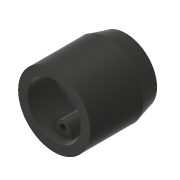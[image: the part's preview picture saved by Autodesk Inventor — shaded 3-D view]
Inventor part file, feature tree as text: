
AUTODESK INVENTOR PART (.ipt)
format: ipt  version: 2017 (Build 210142000, 142)  size: 183,296 bytes
history: native  units: in
note: dims shown in document units (in); Inventor stores cm internally (conversion verified against a paired STEP export)
features: extrude x9, sketch x9, reference x5, other x4, chamfer x1
ambient origin geometry x8: Origin, YZ Plane, XZ Plane, XY Plane, X Axis, Y Axis, Z Axis, Center Point
bodies: Solid1 (feature_tree)
feature tree (28):
  extrude  "Extrusion1"  Depth=1.0in TaperAngle=0.0deg
  extrude  "Extrusion3"  Depth=0.125in TaperAngle=0.0deg
  extrude  "Extrusion4"  Depth=0.75in
  extrude  "Extrusion5"  Depth=0.15in TaperAngle=0.0deg
  sketch  "Sketch7"  dims[d24=0.15in d25=0.0in d26=0.325in d27=0.0in]
  extrude  "Extrusion8"  Depth=0.325in TaperAngle=0.0deg
  extrude  "Extrusion9"  Depth=0.1in
  extrude  "Extrusion10"  Depth=0.25in TaperAngle=15.0deg
  extrude  "Extrusion11"  Depth=0.1in
  chamfer  "Chamfer1"  Distance=0.234in
  extrude  "Extrusion13"  Depth=0.25in
  sketch  "Sketch1"  dims[d0=1.0in d1=1.0in d2=0.0in]
  sketch  "Sketch3"  dims[d6=0.75in d7=0.125in d8=0.0in]
  sketch  "Sketch4"  dims[d11=0.2084in d12=0.0in d13=0.75in]
  reference  "Reference1"
  sketch  "Sketch5"  dims[d14=0.45in d15=0.0in d22=0.15in d23=0.0in]
  sketch  "Sketch8"  dims[d28=0.1in d29=0.1in]
  sketch  "Sketch9"  dims[d30=0.3in d31=0.0in d37=0.25in d38=0.125in d39=15.0deg]
  reference  "Reference2"
  reference  "Reference3"
  sketch  "Sketch10"  dims[d40=0.29in d41=0.1in]
  reference  "Reference4"
  reference  "Reference5"
  sketch  "Sketch12"  dims[d42=0.1in d43=0.234in d44=0.234in d45=0.25in d46=0.0in d47=0.36in]
  parser-record x1  (decoder bookkeeping rows leaked as tree rows — omitted from the tree; the rows remain in map.json)
  other  "Assembly1.iam"
  other  "Holder:1"
  other  "Cap Top Cap:1"
note: 1 file-system path scrubbed to <path> (originals preserved in map.json)
